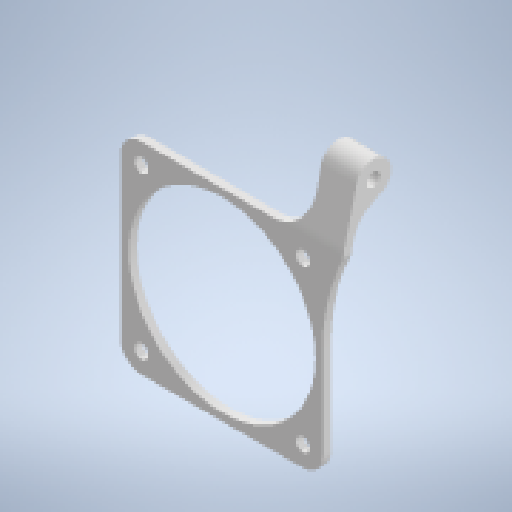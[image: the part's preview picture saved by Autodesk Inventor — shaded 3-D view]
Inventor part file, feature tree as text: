
AUTODESK INVENTOR PART (.ipt)
format: ipt  version: 2023 (Build 270158000, 158)  size: 433,152 bytes
history: native  units: mm
features: sketch x7, other x6, extrude x5, reference x3, fillet x2, revolve x2, pattern_circular x1, plane x1
ambient origin geometry x8: Origin, YZ Plane, XZ Plane, XY Plane, X Axis, Y Axis, Z Axis, Center Point
bodies: Solid1 (feature_tree)
feature tree (27):
  extrude  "Extrusion1"  Depth=40.0mm
  extrude  "Extrusion2"  Depth=4.0mm
  fillet  "Fillet1"  Radius=4.0mm
  fillet  "Fillet2"  Radius=4.0mm
  extrude  "Extrusion3"  Depth=8.0mm
  extrude  "Extrusion4"  Depth=3.0mm
  extrude  "Extrusion5"  Depth=2.7mm
  pattern_circular  "Circular Pattern1"  Count=4  [1 undecoded]
  plane  "Work Plane1"
  revolve  "Revolution1"  [1 undecoded]
  revolve  "Revolution2"  [1 undecoded]
  sketch  "Sketch1"  dims[d0=40.0mm d1=40.0mm]
  sketch  "Sketch3"  dims[d2=4.0mm d3=4.0mm d4=4.0mm d5=4.0mm]
  reference  "Reference1"
  reference  "Reference2"
  sketch  "Sketch4"  dims[d6=38.0mm d7=8.0mm]
  reference  "Reference3"
  sketch  "Sketch5"  dims[d8=14.0mm d9=3.0mm]
  sketch  "Sketch6"  dims[d10=1.6mm d11=0.0mm d15=2.7mm]
  sketch  "Sketch7"  dims[d16=4.1mm d17=2.8mm d18=0.0mm d19=0.0mm d20=40.0mm]
  other  "2D Equation Curve1"
  sketch  "Sketch8"  dims[d21=7.25mm d22=1.6mm d23=0.0mm d24=38.0mm d25=10.0mm d26=0.0mm d27=45.0deg d28=2.0mm d29=10.0mm d30=0.0mm d31=60.0mm d32=360.0deg d34=-20.0mm d36=12.5mm d42=0.0mm d43=27.464014mm d45=1.6mm d46=90.0deg d47=0.0mm d48=25.118864mm d49=10.0mm d50=15.707975mm d51=90.0deg]
  other  "2D Equation Curve2"
  other  "<userpath>\Desktop\Another3dPrinterShroud\MODELS\ENDER 3 ASSEMBLY ALTDUCT.iam"
  other  "ENDER 3 ASSEMBLY ALTDUCT.iam"
  other  "5015 RADIAL FAN:2"
  other  "FRONTPLATE:1"
note: 3 required parameter values undecoded (feature->parameter linkage not recoverable at this tier; creation-order binding heuristic only, values carry confidence <= 0.55)